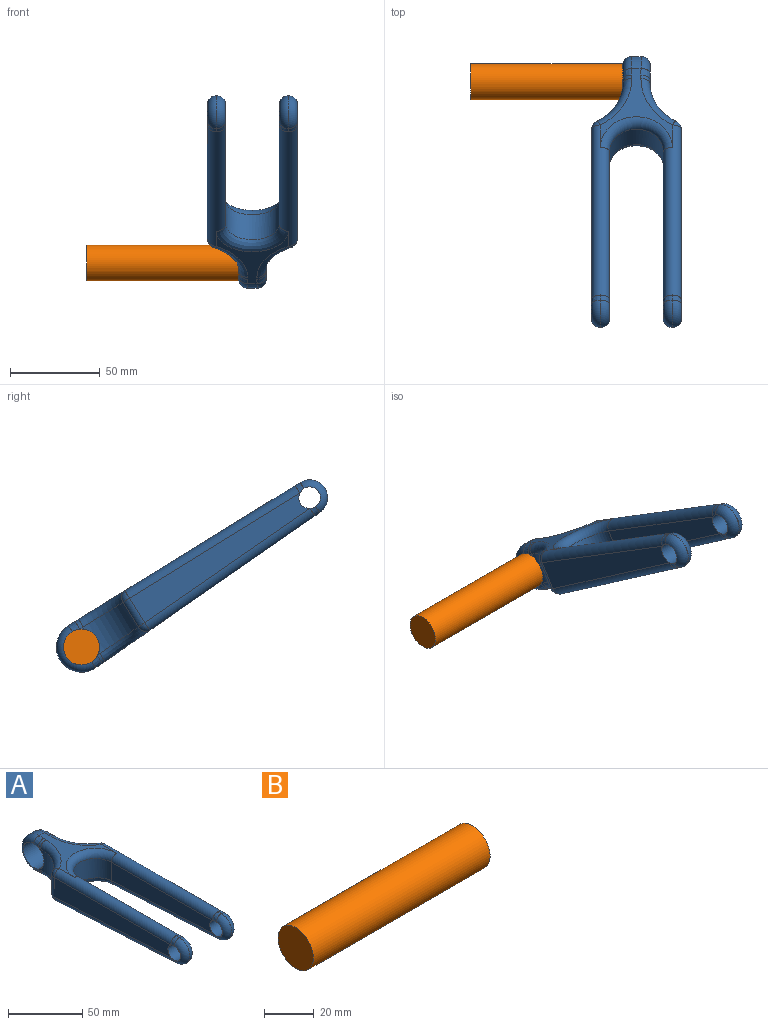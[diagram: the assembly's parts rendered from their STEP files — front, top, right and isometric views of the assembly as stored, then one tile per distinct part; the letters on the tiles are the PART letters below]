
ASSEMBLY  parts=2 mates=1
PART A: 61 faces, bbox 50.5x177.6x30.3 mm
  f0: plane 1.85x1.31mm, normal (-1,0,0), area 1mm2, adj f36,f40,f58
  f1: plane 1.85x1.31mm, normal (1,0,0), area 1mm2, adj f39,f40,f49
  f2: plane 51.2x40mm, normal (0,-0.05,-1), area 451.4mm2, adj f3,f25,f31,f35,f47,f49,f50,f56
  f3: cylinder r=14mm len=28mm, axis (-1,0,0), area 232.6mm2, adj f2,f4,f45,f54
  f4: plane 51.67x40mm, normal (0,0,1), area 453.1mm2, adj f3,f22,f27,f32,f41,f42,f43,f51
  f5: plane 3.31x0.2mm, normal (0,-0.05,-1), area 0.3mm2, adj f11,f30,f34
  f6: plane 3.32x0.2mm, normal (0,0,1), area 0.3mm2, adj f11,f28,f33
  f7: plane 3.32x0.2mm, normal (0,0,1), area 0.3mm2, adj f8,f19,f23
  f8: cylinder r=10mm len=19.99mm, axis (-1,0,0), area 6.2mm2, adj f7,f9,f18,f20
  f9: plane 3.31x0.2mm, normal (0,-0.05,-1), area 0.3mm2, adj f8,f21,f24
  f10: cylinder r=6mm len=12mm, axis (-1,0,0), area 377mm2, adj f13,f15,f18,f19,f20,f21,f23,f24
  f11: cylinder r=10mm len=19.99mm, axis (-1,0,0), area 6.2mm2, adj f5,f6,f26,f29
  f12: cylinder r=6mm len=12mm, axis (-1,0,0), area 377mm2, adj f14,f16,f26,f28,f29,f30,f33,f34
  f13: plane 111.63x16.06mm, normal (1,0,0), area 1442.3mm2, adj f10,f22,f25,f46
  f14: plane 111.63x16.06mm, normal (-1,0,0), area 1442.3mm2, adj f12,f32,f35,f57
  f15: plane 96.94x15.29mm, normal (-1,0,0), area 1212.1mm2, adj f10,f17,f22,f25
  f16: plane 96.94x15.29mm, normal (1,0,0), area 1212.1mm2, adj f12,f17,f32,f35
  f17: cylinder r=15mm len=30mm, axis (0,0,1), area 752mm2, adj f15,f16,f27,f31
  f18: torus R=5mm, axis (1,0,0), area 181.4mm2, adj f8,f10,f19,f21
  f19: bspline ~5.25x5.23mm, area 23.8mm2, adj f7,f10,f18,f22
  f20: torus R=5mm, axis (-1,0,0), area 181.4mm2, adj f8,f10,f23,f24
  f21: bspline ~5.24x5.23mm, area 23.8mm2, adj f9,f10,f18,f25
  f22: cylinder r=5mm len=111.36mm, axis (0,1,0), area 1633.9mm2, adj f4,f13,f15,f19,f23,f27,f44
  f23: bspline ~5.25x5.23mm, area 23.8mm2, adj f7,f10,f20,f22
  f24: bspline ~5.24x5.23mm, area 23.8mm2, adj f9,f10,f20,f25
  f25: cylinder r=5mm len=111.89mm, axis (0,-1,0.05), area 1640.3mm2, adj f2,f13,f15,f21,f24,f31,f48
  f26: torus R=5mm, axis (1,0,0), area 181.4mm2, adj f11,f12,f28,f30
  f27: torus R=20mm, axis (0,0,1), area 414.9mm2, adj f4,f17,f22,f32
  f28: bspline ~5.25x5.23mm, area 23.8mm2, adj f6,f12,f26,f32
  f29: torus R=5mm, axis (-1,0,0), area 181.4mm2, adj f11,f12,f33,f34
  f30: bspline ~5.24x5.23mm, area 23.8mm2, adj f5,f12,f26,f35
  f31: bspline ~40x19.99mm, area 407.4mm2, adj f2,f17,f25,f35
  f32: cylinder r=5mm len=111.36mm, axis (0,1,0), area 1633.9mm2, adj f4,f14,f16,f27,f28,f33,f55
  f33: bspline ~5.25x5.23mm, area 23.8mm2, adj f6,f12,f29,f32
  f34: bspline ~5.24x5.23mm, area 23.8mm2, adj f5,f12,f29,f35
  f35: cylinder r=5mm len=111.89mm, axis (0,1,-0.05), area 1640.3mm2, adj f2,f14,f16,f30,f31,f34,f59
  f36: cylinder r=30mm len=25.98mm, axis (0,0,1), area 495.3mm2, adj f0,f37,f40,f53,f57,f60
  f37: plane 2.31x1.55mm, normal (-1,0,0), area 1.6mm2, adj f36,f40,f51
  f38: plane 2.31x1.55mm, normal (1,0,0), area 1.6mm2, adj f39,f40,f41
  f39: cylinder r=30mm len=25.98mm, axis (0,0,1), area 495.3mm2, adj f1,f38,f40,f42,f46,f50
  f40: cylinder r=10mm len=20mm, axis (-1,0,0), area 942.5mm2, adj f0,f1,f36,f37,f38,f39,f43,f45
  f41: cylinder r=5mm len=5mm, axis (0,1,0), area 18.2mm2, adj f4,f38,f42,f43
  f42: torus R=35mm, axis (0,0,1), area 261.7mm2, adj f4,f39,f41,f44
  f43: bspline ~5x5mm, area 31.3mm2, adj f4,f40,f41,f45
  f44: sphere r=5mm, area 26.2mm2, adj f22,f42,f46
  f45: torus R=9mm, axis (1,0,0), area 275.1mm2, adj f3,f40,f43,f47
  f46: cylinder r=5mm len=16.06mm, axis (0,0,1), area 84.1mm2, adj f13,f39,f44,f48
  f47: bspline ~5.95x5.43mm, area 31.3mm2, adj f2,f40,f45,f49
  f48: sphere r=5mm, area 26.8mm2, adj f25,f46,f50
  f49: cylinder r=5mm len=5.09mm, axis (0,1,-0.05), area 14.5mm2, adj f1,f2,f47,f50
  f50: bspline ~37.16x21.25mm, area 265.9mm2, adj f2,f39,f48,f49
  f51: cylinder r=5mm len=5mm, axis (0,-1,0), area 18.2mm2, adj f4,f37,f52,f53
  f52: bspline ~5x5mm, area 31.3mm2, adj f4,f40,f51,f54
  f53: torus R=35mm, axis (0,0,1), area 261.7mm2, adj f4,f36,f51,f55
  f54: torus R=9mm, axis (-1,0,0), area 275.1mm2, adj f3,f40,f52,f56
  f55: sphere r=5mm, area 26.2mm2, adj f32,f53,f57
  f56: bspline ~5.95x5.43mm, area 31.3mm2, adj f2,f40,f54,f58
  f57: cylinder r=5mm len=16.06mm, axis (0,0,1), area 84.1mm2, adj f14,f36,f55,f59
  f58: cylinder r=5mm len=5.09mm, axis (0,-1,0.05), area 14.5mm2, adj f0,f2,f56,f60
  f59: sphere r=5mm, area 26.8mm2, adj f35,f57,f60
  f60: bspline ~37.16x21.25mm, area 265.9mm2, adj f2,f36,f58,f59
PART B: 3 faces, bbox 100x20x20 mm
  f0: cylinder r=10mm len=100mm, axis (-1,0,0), area 6283.2mm2, adj f1,f2
  f1: plane 20x20mm, normal (1,0,0), area 314.2mm2, adj f0
  f2: plane 20x20mm, normal (-1,0,0), area 314.2mm2, adj f0
PLACE A rot(axis=(-1,0,0),31.7deg) t=(54.29,-16.79,-31.11)mm
PLACE B t=(12.07,0.08,-10.34)mm fixed
MATE revolute A.f54 <-> B.f0  axis (-1,0,0) through (62.07,0.08,-10.34)mm
